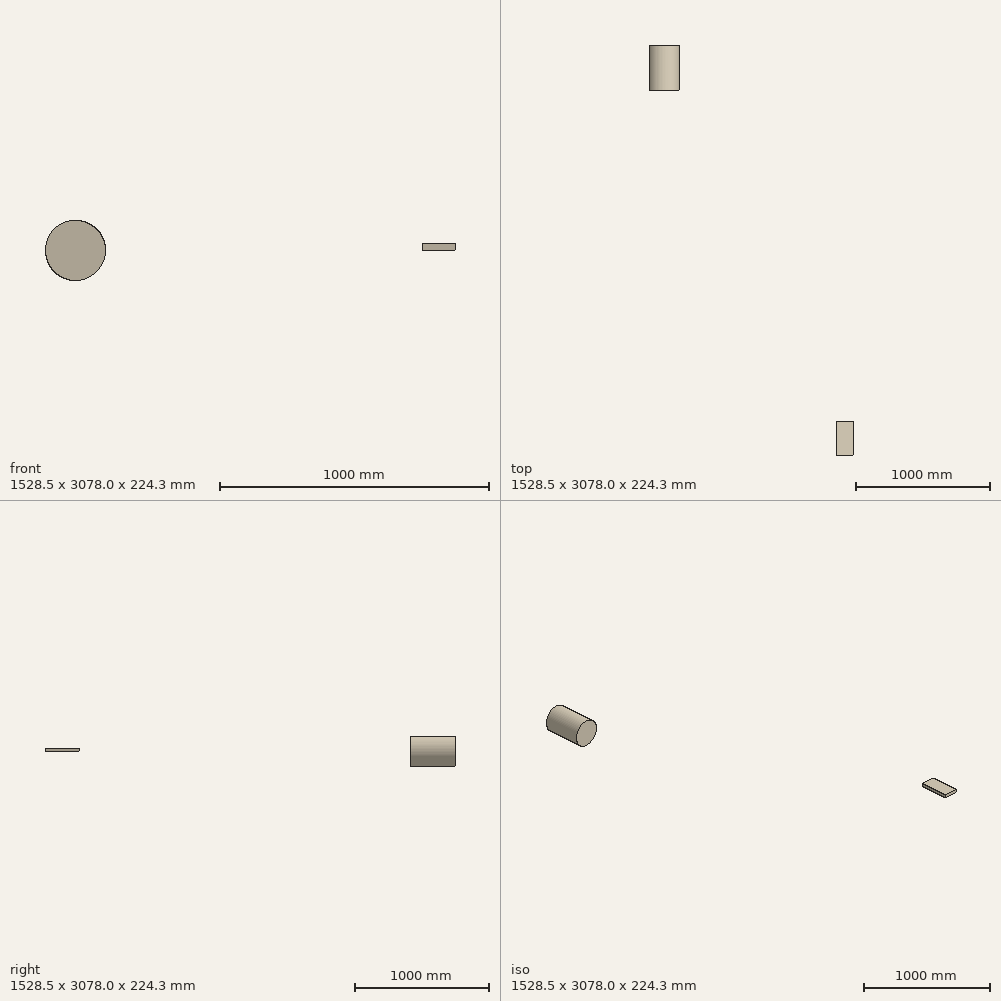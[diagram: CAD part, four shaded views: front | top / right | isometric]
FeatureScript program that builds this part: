
annotation { "Feature Type Name" : "Feature", "Feature Type Description" : "" }
export const myFeature = defineFeature(function(context is Context, id is Id, definition is map)
    precondition{}
    {
        {
            var Q0;
            Q0=qCreatedBy(makeId("Front.planeOp"),FACE);
            var sketch = newSketch(context, id + "F0", { "sketchPlane" : qUnion([Q0])});
            skCircle(sketch, "E0", {"center": v(0, 0) * mm, "radius": 112.14 * mm});
            skSolve(sketch);
        }
        {
            var Q0;
            Q0=makeQuery(id+"F0.imprint","IMPRINT",FACE,{"disambiguationData":[TD([[makeQuery(id+"F0.imprint","IMPRINT",EDGE,{"derivedFrom":sQuery(id+"F0.wireOp",EDGE,"E0")}),1.0]])]});
            var Q1;
            Q1=sQuery(id+"F0.wireOp",EDGE,"E0");
            extrude(context, id + "F3", {"entities" : qUnion([Q0]), "surfaceEntities" : qUnion([Q1]), "depth" : 337.09 * mm});
        }
        {
            var Q0;
            Q0=qCreatedBy(makeId("Top.planeOp"),FACE);
            var sketch = newSketch(context, id + "F1", { "sketchPlane" : qUnion([Q0])});
            skLineSegment(sketch, "E1.bottom", {"start": v(1416.36, -3078) * mm, "end": v(1292.53, -3078) * mm});
            skLineSegment(sketch, "E1.top", {"start": v(1416.36, -2820.37) * mm, "end": v(1292.53, -2820.37) * mm});
            skLineSegment(sketch, "E1.left", {"start": v(1416.36, -3078) * mm, "end": v(1416.36, -2820.37) * mm});
            skLineSegment(sketch, "E1.right", {"start": v(1292.53, -3078) * mm, "end": v(1292.53, -2820.37) * mm});
            skSolve(sketch);
        }
        {
            var Q0;
            Q0=makeQuery(id+"F1.imprint","IMPRINT",FACE,{"disambiguationData":[TD([[makeQuery(id+"F1.imprint","IMPRINT",EDGE,{"derivedFrom":sQuery(id+"F1.wireOp",EDGE,"E1.bottom")}),-1.0]])]});
            extrude(context, id + "F2", {"entities" : qUnion([Q0]), "depth" : 25 * mm});
        }
    });
